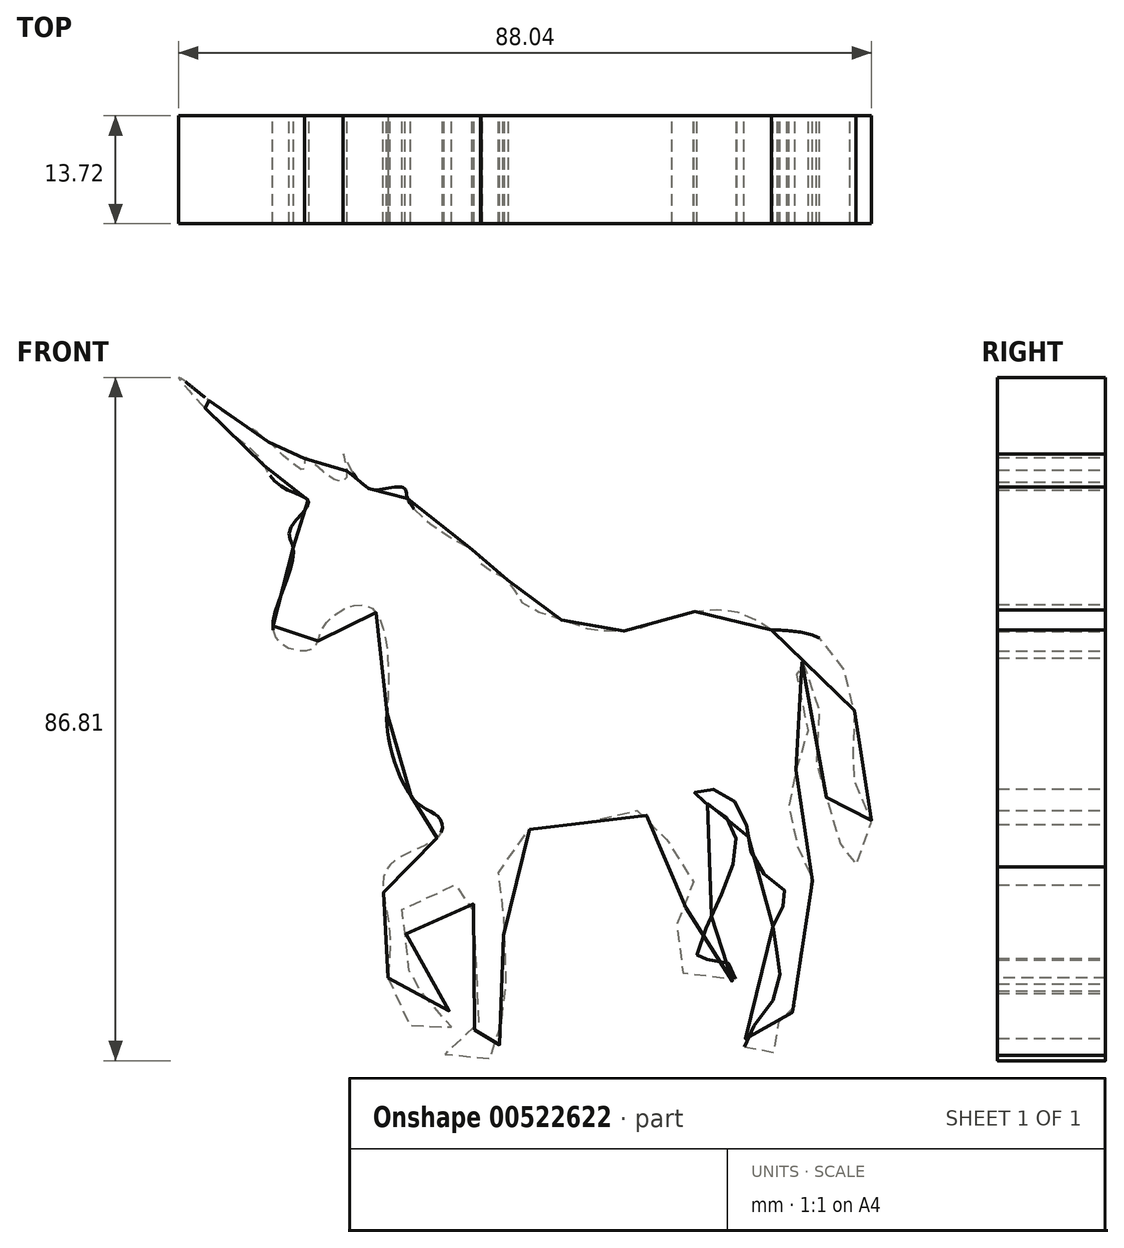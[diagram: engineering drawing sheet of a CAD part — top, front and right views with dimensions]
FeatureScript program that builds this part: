
annotation { "Feature Type Name" : "Feature", "Feature Type Description" : "" }
export const myFeature = defineFeature(function(context is Context, id is Id, definition is map)
    precondition{}
    {
        {
            var Q0;
            Q0=qCreatedBy(makeId("Front.planeOp"),FACE);
            var sketch = newSketch(context, id + "F0", { "sketchPlane" : qUnion([Q0])});
            skFitSpline(sketch, "E0", {"points": [v(48.69, 17.96) * mm, v(43.35, 20.4) * mm, v(35.57, 19.42) * mm, v(31.2, 17.96) * mm, v(25.86, 17.96) * mm, v(22.94, 18.93) * mm, v(17.11, 21.36) * mm, v(15.17, 24.28) * mm, v(11.77, 26.22) * mm, v(11.77, 27.2) * mm, v(7.88, 29.62) * mm, v(2.54, 34.48) * mm, v(2.05, 35.94) * mm, v(0, 35.94) * mm, v(-3.3, 36.42) * mm, v(-5.72, 40.3) * mm, v(-5.23, 37.4) * mm, v(-6.7, 36.9) * mm, v(-10.58, 39.82) * mm, v(-10.58, 38.37) * mm, v(-13, 39.82) * mm, v(-16.9, 43.22) * mm, v(-20.3, 45.17) * mm, v(-26.6, 50.03) * mm, v(-20.78, 43.71) * mm, v(-16.4, 39.82) * mm, v(-14.46, 36.9) * mm, v(-11.06, 34.97) * mm, v(-10.1, 34) * mm, v(-12.52, 30.6) * mm, v(-12.03, 28.17) * mm, v(-13.98, 21.36) * mm, v(-13.98, 16.5) * mm, v(-9.6, 15.53) * mm, v(-8.15, 18.45) * mm, v(-2.32, 20.88) * mm, v(0, 10.2) * mm, v(0, 4.36) * mm, v(3.51, -3.9) * mm, v(6.43, -5.84) * mm, v(6.43, -8.27) * mm, v(0, -12.16) * mm, v(0, -18.96) * mm, v(0, -26.24) * mm], "startDerivative": vector(-181.23, 118.8) * mm, "endDerivative": vector(-19.78, -238.89) * mm});
            skFitSpline(sketch, "E1", {"points": [v(0, -26.24) * mm, v(2.28, -31.92) * mm, v(7.66, -33.53) * mm, v(6.04, -28.16) * mm, v(2.28, -28.16) * mm, v(2.82, -23.88) * mm, v(2.28, -16.33) * mm, v(10.34, -14.71) * mm, v(10.88, -16.33) * mm, v(10.88, -23.88) * mm, v(11.96, -30.3) * mm, v(8.73, -35.15) * mm, v(7.12, -36.22) * mm, v(13.57, -36.22) * mm, v(14.1, -33) * mm, v(15.18, -30.3) * mm, v(14.65, -23.88) * mm, v(14.65, -15.79) * mm, v(14.1, -12.16) * mm, v(18.4, -7.19) * mm, v(24.32, -6.65) * mm, v(31.85, -5.04) * mm, v(34, -7.19) * mm, v(38.3, -12.16) * mm, v(38.3, -16.33) * mm, v(36.15, -21.17) * mm, v(38.3, -26.24) * mm, v(44.22, -26.24) * mm, v(42.07, -23.88) * mm, v(39.38, -23.88) * mm, v(41.53, -17.4) * mm, v(44.22, -9.34) * mm, v(42.07, -5.04) * mm, v(38.84, -2.89) * mm, v(41.53, -2.35) * mm, v(45.3, -6.11) * mm, v(46.9, -12.16) * mm, v(50.67, -15.79) * mm, v(49.06, -19.02) * mm, v(49.6, -23.88) * mm, v(48.52, -29.77) * mm, v(45.3, -35.15) * mm, v(49.06, -35.68) * mm, v(49.6, -31.92) * mm, v(51.2, -30.84) * mm, v(52.28, -23.88) * mm, v(53.9, -15.25) * mm, v(53.36, -12.16) * mm, v(51.2, -7.19) * mm, v(51.74, 0) * mm, v(53.36, 5.18) * mm, v(51.74, 14.32) * mm, v(54.43, 10.2) * mm, v(54.43, 0) * mm, v(56.58, -5.57) * mm, v(58.73, -12.16) * mm, v(61.42, -6.65) * mm, v(58.73, 0) * mm, v(59.27, 3.03) * mm, v(58.73, 10.2) * mm, v(55.5, 16.47) * mm, v(48.69, 17.96) * mm], "startDerivative": vector(53.23, -347.29) * mm, "endDerivative": vector(-408.58, 18.45) * mm});
            skSolve(sketch);
        }
        {
            var Q0;
            Q0 = qSketchRegion(id + "F0", true);
            extrude(context, id + "F1", {"entities" : qUnion([Q0]), "oppositeDirection" : true, "depth" : 13.72 * mm, "offsetDistance" : 25.4 * mm});
        }
    });
